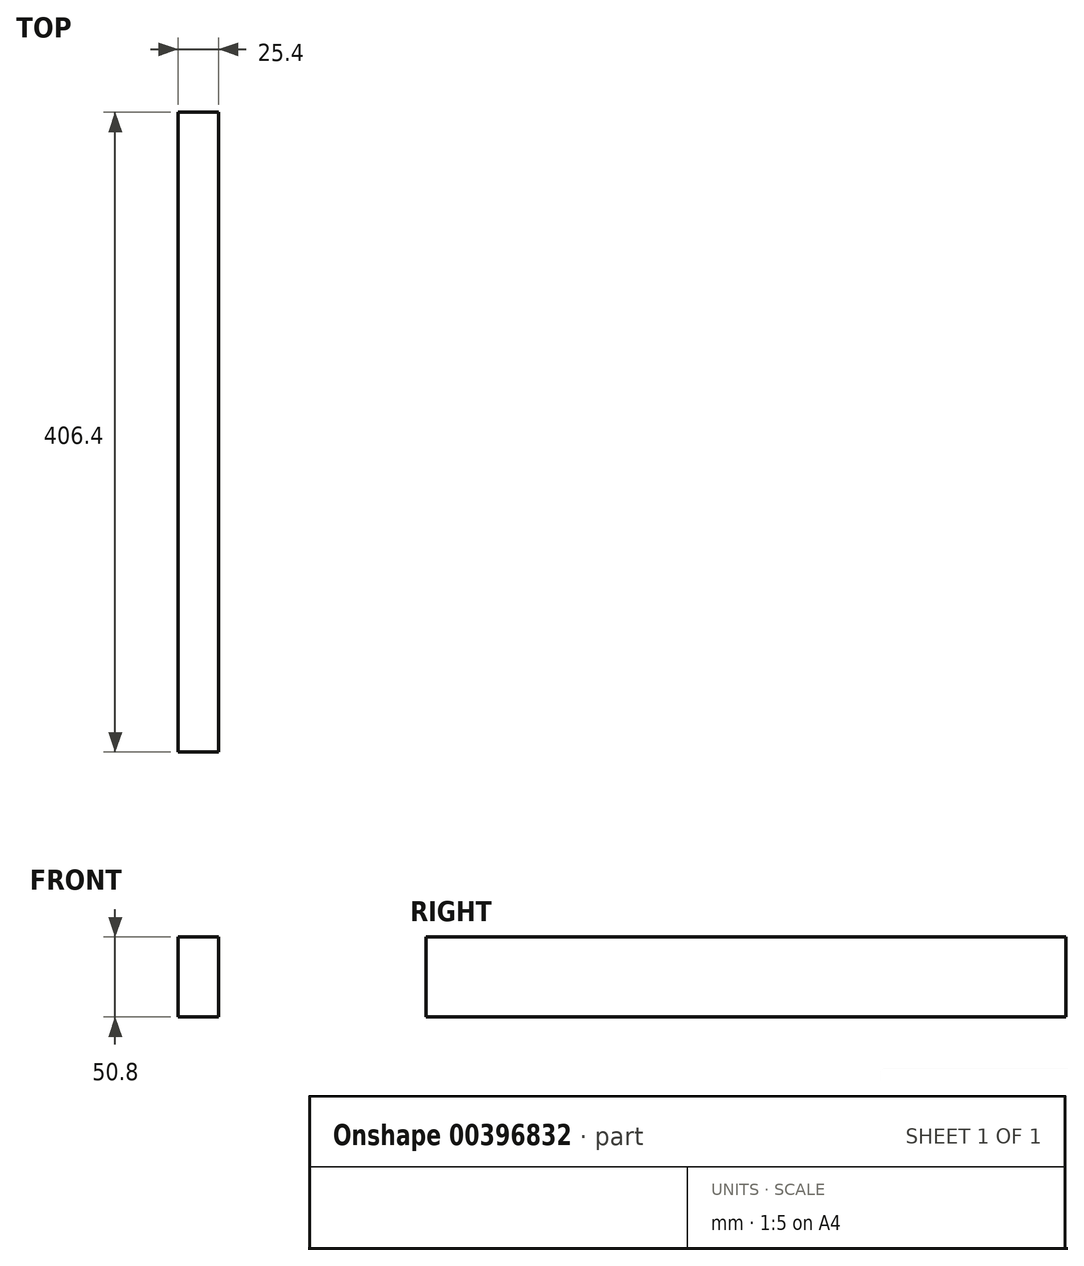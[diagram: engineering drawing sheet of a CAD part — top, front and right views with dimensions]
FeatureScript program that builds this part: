
annotation { "Feature Type Name" : "Feature", "Feature Type Description" : "" }
export const myFeature = defineFeature(function(context is Context, id is Id, definition is map)
    precondition{}
    {
        {
            var Q0;
            Q0=qCreatedBy(makeId("Right.planeOp"),FACE);
            var sketch = newSketch(context, id + "F0", { "sketchPlane" : qUnion([Q0])});
            skLineSegment(sketch, "E0.bottom", {"start": v(-203.2, 25.4) * mm, "end": v(203.2, 25.4) * mm});
            skLineSegment(sketch, "E0.top", {"start": v(-203.2, -25.4) * mm, "end": v(203.2, -25.4) * mm});
            skLineSegment(sketch, "E0.left", {"start": v(-203.2, 25.4) * mm, "end": v(-203.2, -25.4) * mm});
            skLineSegment(sketch, "E0.right", {"start": v(203.2, 25.4) * mm, "end": v(203.2, -25.4) * mm});
            skPoint(sketch, "E0.middle", {"position": v(0, 0) * mm});
            skSolve(sketch);
        }
        {
            var Q0;
            Q0=makeQuery(id+"F0.imprint","IMPRINT",FACE,{"disambiguationData":[TD([[makeQuery(id+"F0.imprint","IMPRINT",EDGE,{"derivedFrom":sQuery(id+"F0.wireOp",EDGE,"E0.bottom")}),-1.0]])]});
            extrude(context, id + "F1", {"entities" : qUnion([Q0]), "depth" : 25.4 * mm});
        }
    });
